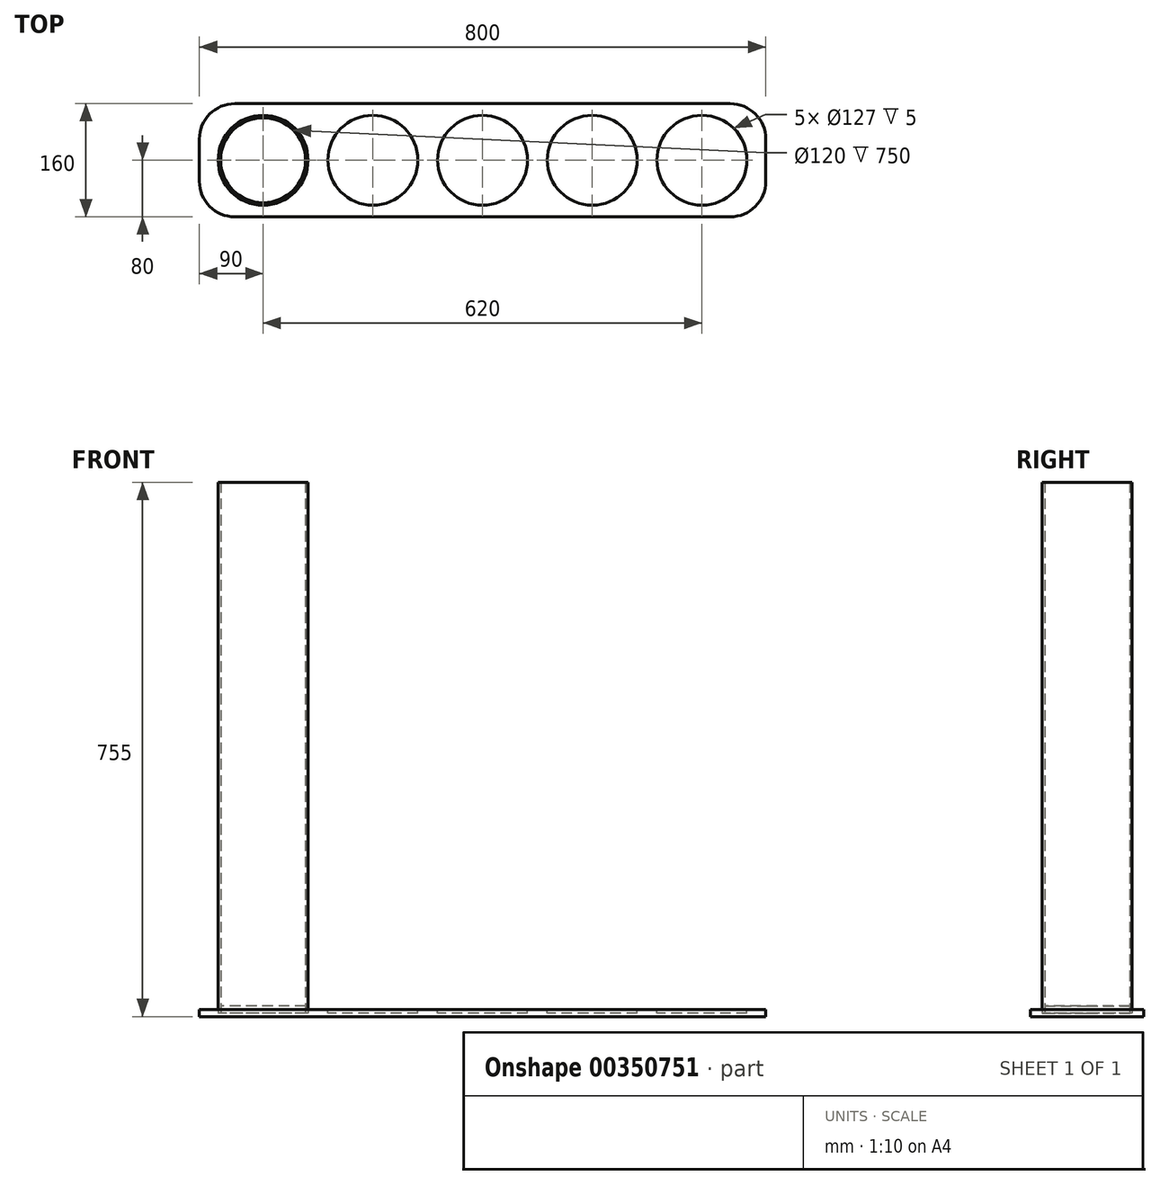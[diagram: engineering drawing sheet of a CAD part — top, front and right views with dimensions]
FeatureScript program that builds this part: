
annotation { "Feature Type Name" : "Feature", "Feature Type Description" : "" }
export const myFeature = defineFeature(function(context is Context, id is Id, definition is map)
    precondition{}
    {
        {
            var Q0;
            Q0=qCreatedBy(makeId("Top.planeOp"),FACE);
            var sketch = newSketch(context, id + "F0", { "sketchPlane" : qUnion([Q0])});
            skLineSegment(sketch, "E0.bottom", {"start": v(400, 80) * mm, "end": v(-400, 80) * mm});
            skLineSegment(sketch, "E0.top", {"start": v(400, -80) * mm, "end": v(-400, -80) * mm});
            skLineSegment(sketch, "E0.left", {"start": v(400, 80) * mm, "end": v(400, -80) * mm});
            skLineSegment(sketch, "E0.right", {"start": v(-400, 80) * mm, "end": v(-400, -80) * mm});
            skPoint(sketch, "E0.middle", {"position": v(0, 0) * mm});
            skSolve(sketch);
        }
        {
            var Q0;
            Q0=makeQuery(id+"F0.imprint","IMPRINT",FACE,{"disambiguationData":[TD([[makeQuery(id+"F0.imprint","IMPRINT",EDGE,{"derivedFrom":sQuery(id+"F0.wireOp",EDGE,"E0.bottom")}),1.0]])]});
            extrude(context, id + "F1", {"entities" : qUnion([Q0]), "depth" : 10 * mm});
        }
        {
            var Q0;
            Q0=makeQuery(id+"F1.opExtrude","CAP_FACE",FACE,{"disambiguationData":[OSD([sQuery(id+"F0.wireOp",EDGE,"E0.bottom"),sQuery(id+"F0.wireOp",EDGE,"E0.top"),sQuery(id+"F0.wireOp",EDGE,"E0.left"),sQuery(id+"F0.wireOp",EDGE,"E0.right")])],"isStart":false});
            var sketch = newSketch(context, id + "F2", { "sketchPlane" : qUnion([Q0])});
            skCircle(sketch, "E1", {"center": v(-310, 0) * mm, "radius": 63.5 * mm});
            skCircle(sketch, "E2", {"center": v(-155, 0) * mm, "radius": 63.5 * mm});
            skCircle(sketch, "E3", {"center": v(0, 0) * mm, "radius": 63.5 * mm});
            skCircle(sketch, "E4", {"center": v(155, 0) * mm, "radius": 63.5 * mm});
            skCircle(sketch, "E5", {"center": v(310, 0) * mm, "radius": 63.5 * mm});
            skLineSegment(sketch, "E6", {"start": v(-310, 0) * mm, "end": v(-155, 0) * mm, "construction": true});
            skLineSegment(sketch, "E7", {"start": v(-155, 0) * mm, "end": v(0, 0) * mm, "construction": true});
            skLineSegment(sketch, "E8", {"start": v(0, 0) * mm, "end": v(155, 0) * mm, "construction": true});
            skLineSegment(sketch, "E9", {"start": v(155, 0) * mm, "end": v(310, 0) * mm, "construction": true});
            skSolve(sketch);
        }
        {
            var Q0;
            Q0=makeQuery(id+"F2.imprint","IMPRINT",FACE,{"disambiguationData":[TD([[makeQuery(id+"F2.imprint","IMPRINT",EDGE,{"derivedFrom":sQuery(id+"F2.wireOp",EDGE,"E1")}),1.0]])]});
            var Q1;
            Q1=makeQuery(id+"F2.imprint","IMPRINT",FACE,{"disambiguationData":[TD([[makeQuery(id+"F2.imprint","IMPRINT",EDGE,{"derivedFrom":sQuery(id+"F2.wireOp",EDGE,"E2")}),1.0]])]});
            var Q2;
            Q2=makeQuery(id+"F2.imprint","IMPRINT",FACE,{"disambiguationData":[TD([[makeQuery(id+"F2.imprint","IMPRINT",EDGE,{"derivedFrom":sQuery(id+"F2.wireOp",EDGE,"E3")}),1.0]])]});
            var Q3;
            Q3=makeQuery(id+"F2.imprint","IMPRINT",FACE,{"disambiguationData":[TD([[makeQuery(id+"F2.imprint","IMPRINT",EDGE,{"derivedFrom":sQuery(id+"F2.wireOp",EDGE,"E4")}),1.0]])]});
            var Q4;
            Q4=makeQuery(id+"F2.imprint","IMPRINT",FACE,{"disambiguationData":[TD([[makeQuery(id+"F2.imprint","IMPRINT",EDGE,{"derivedFrom":sQuery(id+"F2.wireOp",EDGE,"E5")}),1.0]])]});
            extrude(context, id + "F3", {"entities" : qUnion([Q0, Q1, Q2, Q3, Q4]), "operationType" : NewBodyOperationType.REMOVE, "oppositeDirection" : true, "depth" : 5 * mm});
        }
        {
            var Q0;
            Q0=makeQuery(id+"F1.opExtrude","SWEPT_EDGE",EDGE,{"disambiguationData":[OSD([sQuery(id+"F0.wireOp",EDGE,"E0.top"),sQuery(id+"F0.wireOp",EDGE,"E0.right")])]});
            var Q1;
            Q1=makeQuery(id+"F1.opExtrude","SWEPT_EDGE",EDGE,{"disambiguationData":[OSD([sQuery(id+"F0.wireOp",EDGE,"E0.top"),sQuery(id+"F0.wireOp",EDGE,"E0.left")])]});
            var Q2;
            Q2=makeQuery(id+"F1.opExtrude","SWEPT_EDGE",EDGE,{"disambiguationData":[OSD([sQuery(id+"F0.wireOp",EDGE,"E0.bottom"),sQuery(id+"F0.wireOp",EDGE,"E0.left")])]});
            var Q3;
            Q3=makeQuery(id+"F1.opExtrude","SWEPT_EDGE",EDGE,{"disambiguationData":[OSD([sQuery(id+"F0.wireOp",EDGE,"E0.bottom"),sQuery(id+"F0.wireOp",EDGE,"E0.right")])]});
            fillet(context, id + "F4", {"entities" : qUnion([Q0, Q1, Q2, Q3]), "radius" : 50 * mm, "tangentPropagation" : true, "allowEdgeOverflow" : false});
        }
        {
            var Q0;
            Q0=makeQuery(id+"F3.boolean.opBoolean","COPY",FACE,{"derivedFrom":makeQuery(id+"F3.opExtrude","CAP_FACE",FACE,{"disambiguationData":[OSD([sQuery(id+"F2.wireOp",EDGE,"E1")])],"isStart":false})});
            var sketch = newSketch(context, id + "F5", { "sketchPlane" : qUnion([Q0])});
            skCircle(sketch, "E10", {"center": v(-310, 0) * mm, "radius": 60 * mm});
            skCircle(sketch, "E11", {"center": v(-310, 0) * mm, "radius": 63.5 * mm});
            skSolve(sketch);
        }
        {
            var Q0;
            Q0=makeQuery(id+"F5.imprint","IMPRINT",FACE,{"disambiguationData":[TD([[makeQuery(id+"F5.imprint","IMPRINT",EDGE,{"derivedFrom":sQuery(id+"F5.wireOp",EDGE,"E10")}),1.0]])]});
            extrude(context, id + "F6", {"entities" : qUnion([Q0]), "depth" : 10 * mm});
        }
        {
            var Q0;
            Q0 = qSketchRegion(id + "F5", true);
            extrude(context, id + "F7", {"entities" : qUnion([Q0]), "depth" : 750 * mm});
        }
        {
            var Q0;
            Q0=makeQuery(id+"F6.opExtrude","CAP_FACE",FACE,{"disambiguationData":[OSD([sQuery(id+"F5.wireOp",EDGE,"E10")])],"isStart":false});
            extrude(context, id + "F8", {"entities" : qUnion([Q0]), "depth" : 740 * mm});
        }
    });
